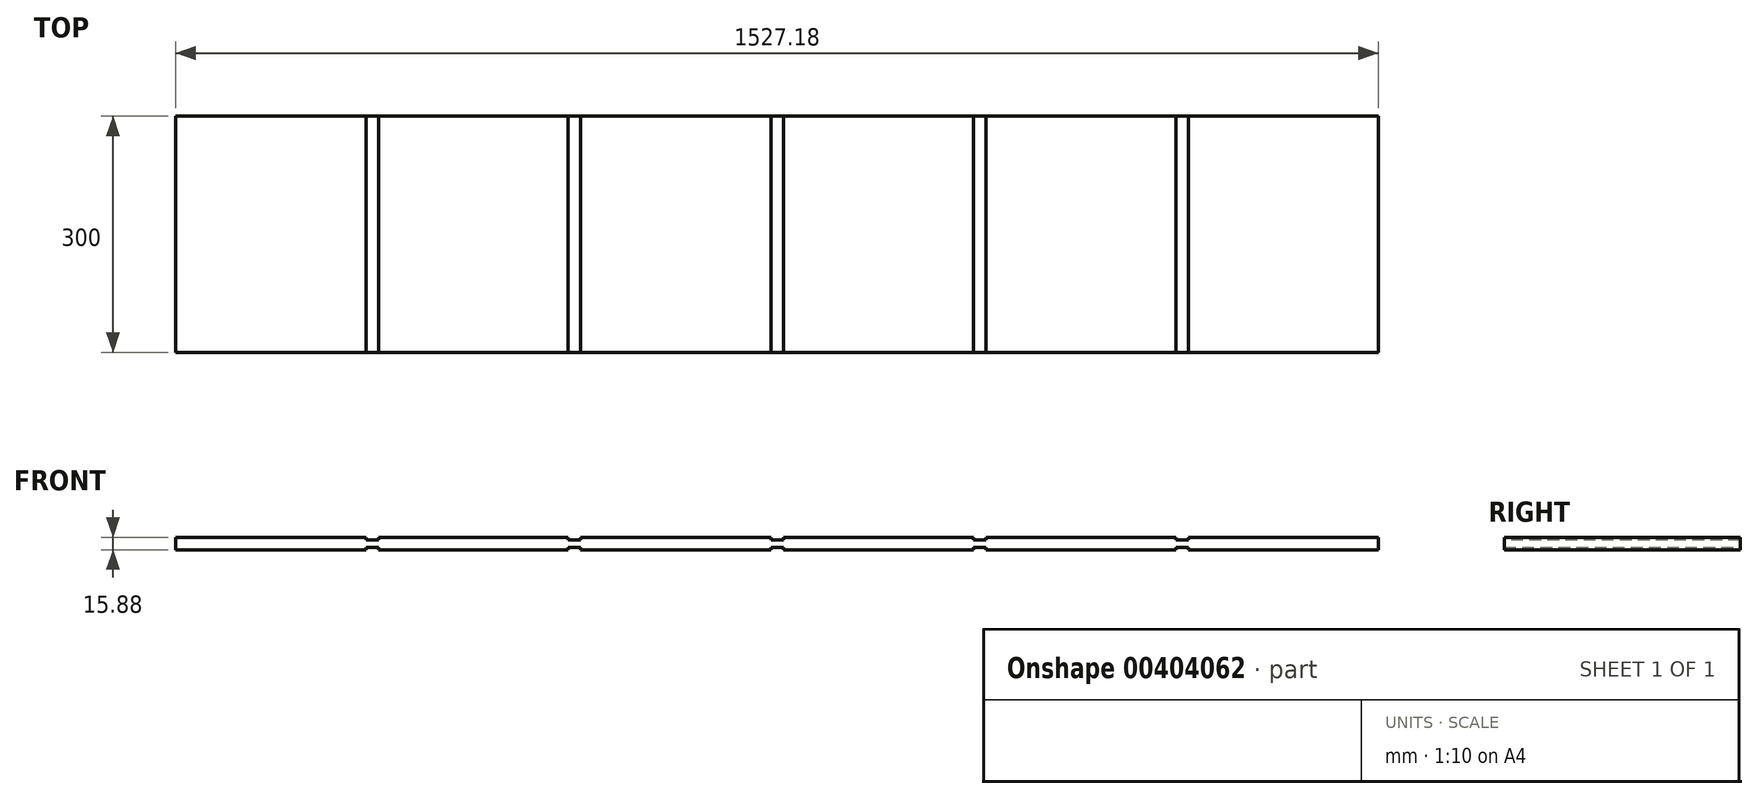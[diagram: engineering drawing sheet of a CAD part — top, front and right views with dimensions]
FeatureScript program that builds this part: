
annotation { "Feature Type Name" : "Feature", "Feature Type Description" : "" }
export const myFeature = defineFeature(function(context is Context, id is Id, definition is map)
    precondition{}
    {
        {
            var Q0;
            Q0=qCreatedBy(makeId("Front.planeOp"),FACE);
            var sketch = newSketch(context, id + "F0", { "sketchPlane" : qUnion([Q0])});
            skLineSegment(sketch, "E0.bottom", {"start": v(-761.76, -27.04) * mm, "end": v(765.42, -27.04) * mm});
            skLineSegment(sketch, "E0.top", {"start": v(-761.76, -42.92) * mm, "end": v(765.42, -42.92) * mm});
            skLineSegment(sketch, "E0.left", {"start": v(-761.76, -27.04) * mm, "end": v(-761.76, -42.92) * mm});
            skLineSegment(sketch, "E0.right", {"start": v(765.42, -27.04) * mm, "end": v(765.42, -42.92) * mm});
            skSolve(sketch);
        }
        {
            var Q0;
            Q0 = qSketchRegion(id + "F0", true);
            extrude(context, id + "F1", {"entities" : qUnion([Q0]), "depth" : 300 * mm});
        }
        {
            var Q0;
            Q0=makeQuery(id+"F1.opExtrude","SWEPT_FACE",FACE,{"disambiguationData":[OSD([sQuery(id+"F0.wireOp",EDGE,"E0.top")])]});
            var sketch = newSketch(context, id + "F2", { "sketchPlane" : qUnion([Q0])});
            skLineSegment(sketch, "E1.bottom", {"start": v(-761.76, 300) * mm, "end": v(-520.46, 300) * mm});
            skLineSegment(sketch, "E1.top", {"start": v(-761.76, 0) * mm, "end": v(-520.46, 0) * mm});
            skLineSegment(sketch, "E1.left", {"start": v(-761.76, 300) * mm, "end": v(-761.76, 0) * mm});
            skLineSegment(sketch, "E1.right", {"start": v(-520.46, 300) * mm, "end": v(-520.46, 0) * mm});
            skLineSegment(sketch, "E2.bottom", {"start": v(-504.58, 300) * mm, "end": v(-263.28, 300) * mm});
            skLineSegment(sketch, "E2.top", {"start": v(-504.58, 0) * mm, "end": v(-263.28, 0) * mm});
            skLineSegment(sketch, "E2.left", {"start": v(-504.58, 300) * mm, "end": v(-504.58, 0) * mm});
            skLineSegment(sketch, "E2.right", {"start": v(-263.28, 300) * mm, "end": v(-263.28, 0) * mm});
            skLineSegment(sketch, "E3.bottom", {"start": v(-247.4, 300) * mm, "end": v(-6.1, 300) * mm});
            skLineSegment(sketch, "E3.top", {"start": v(-247.4, 0) * mm, "end": v(-6.1, 0) * mm});
            skLineSegment(sketch, "E3.left", {"start": v(-247.4, 300) * mm, "end": v(-247.4, 0) * mm});
            skLineSegment(sketch, "E3.right", {"start": v(-6.1, 300) * mm, "end": v(-6.1, 0) * mm});
            skLineSegment(sketch, "E4.bottom", {"start": v(9.77, 300) * mm, "end": v(251.07, 300) * mm});
            skLineSegment(sketch, "E4.top", {"start": v(9.77, 0) * mm, "end": v(251.07, 0) * mm});
            skLineSegment(sketch, "E4.left", {"start": v(9.77, 300) * mm, "end": v(9.77, 0) * mm});
            skLineSegment(sketch, "E4.right", {"start": v(251.07, 300) * mm, "end": v(251.07, 0) * mm});
            skLineSegment(sketch, "E5.bottom", {"start": v(266.94, 300) * mm, "end": v(508.24, 300) * mm});
            skLineSegment(sketch, "E5.top", {"start": v(266.94, 0) * mm, "end": v(508.24, 0) * mm});
            skLineSegment(sketch, "E5.left", {"start": v(266.94, 300) * mm, "end": v(266.94, 0) * mm});
            skLineSegment(sketch, "E5.right", {"start": v(508.24, 300) * mm, "end": v(508.24, 0) * mm});
            skLineSegment(sketch, "E6.bottom", {"start": v(524.12, 300) * mm, "end": v(765.42, 300) * mm});
            skLineSegment(sketch, "E6.top", {"start": v(524.12, 0) * mm, "end": v(765.42, 0) * mm});
            skLineSegment(sketch, "E6.left", {"start": v(524.12, 300) * mm, "end": v(524.12, 0) * mm});
            skLineSegment(sketch, "E6.right", {"start": v(765.42, 300) * mm, "end": v(765.42, 0) * mm});
            skLineSegment(sketch, "E7.bottom", {"start": v(-520.46, 300) * mm, "end": v(-504.58, 300) * mm});
            skLineSegment(sketch, "E7.top", {"start": v(-520.46, 0) * mm, "end": v(-504.58, 0) * mm});
            skLineSegment(sketch, "E8.bottom", {"start": v(-263.28, 300) * mm, "end": v(-247.4, 300) * mm});
            skLineSegment(sketch, "E8.top", {"start": v(-263.28, 0) * mm, "end": v(-247.4, 0) * mm});
            skLineSegment(sketch, "E9.bottom", {"start": v(-6.1, 300) * mm, "end": v(9.77, 300) * mm});
            skLineSegment(sketch, "E9.top", {"start": v(-6.1, 0) * mm, "end": v(9.77, 0) * mm});
            skLineSegment(sketch, "E10.bottom", {"start": v(251.07, 300) * mm, "end": v(266.94, 300) * mm});
            skLineSegment(sketch, "E10.top", {"start": v(251.07, 0) * mm, "end": v(266.94, 0) * mm});
            skLineSegment(sketch, "E11.bottom", {"start": v(508.24, 300) * mm, "end": v(524.12, 300) * mm});
            skLineSegment(sketch, "E11.top", {"start": v(508.24, 0) * mm, "end": v(524.12, 0) * mm});
            skSolve(sketch);
        }
        {
            var Q0;
            Q0=makeQuery(id+"F2.imprint","IMPRINT",FACE,{"disambiguationData":[TD([[makeQuery(id+"F2.imprint","IMPRINT",EDGE,{"derivedFrom":sQuery(id+"F2.wireOp",EDGE,"E8.bottom")}),-1.0]])]});
            var Q1;
            Q1=makeQuery(id+"F2.imprint","IMPRINT",FACE,{"disambiguationData":[TD([[makeQuery(id+"F2.imprint","IMPRINT",EDGE,{"derivedFrom":sQuery(id+"F2.wireOp",EDGE,"E9.bottom")}),-1.0]])]});
            var Q2;
            Q2=makeQuery(id+"F2.imprint","IMPRINT",FACE,{"disambiguationData":[TD([[makeQuery(id+"F2.imprint","IMPRINT",EDGE,{"derivedFrom":sQuery(id+"F2.wireOp",EDGE,"E7.bottom")}),-1.0]])]});
            var Q3;
            Q3=makeQuery(id+"F2.imprint","IMPRINT",FACE,{"disambiguationData":[TD([[makeQuery(id+"F2.imprint","IMPRINT",EDGE,{"derivedFrom":sQuery(id+"F2.wireOp",EDGE,"E10.bottom")}),-1.0]])]});
            var Q4;
            Q4=makeQuery(id+"F2.imprint","IMPRINT",FACE,{"disambiguationData":[TD([[makeQuery(id+"F2.imprint","IMPRINT",EDGE,{"derivedFrom":sQuery(id+"F2.wireOp",EDGE,"E11.bottom")}),-1.0]])]});
            extrude(context, id + "F3", {"entities" : qUnion([Q0, Q1, Q2, Q3, Q4]), "operationType" : NewBodyOperationType.REMOVE, "oppositeDirection" : true, "depth" : 3.17 * mm});
        }
        {
            var Q0;
            Q0=makeQuery(id+"F1.opExtrude","SWEPT_FACE",FACE,{"disambiguationData":[OSD([sQuery(id+"F0.wireOp",EDGE,"E0.bottom")])]});
            var sketch = newSketch(context, id + "F4", { "sketchPlane" : qUnion([Q0])});
            skLineSegment(sketch, "E12.bottom", {"start": v(-520.46, 0) * mm, "end": v(-504.58, 0) * mm});
            skLineSegment(sketch, "E12.top", {"start": v(-520.46, -300) * mm, "end": v(-504.58, -300) * mm});
            skLineSegment(sketch, "E12.left", {"start": v(-520.46, 0) * mm, "end": v(-520.46, -300) * mm});
            skLineSegment(sketch, "E12.right", {"start": v(-504.58, 0) * mm, "end": v(-504.58, -300) * mm});
            skLineSegment(sketch, "E13.bottom", {"start": v(-263.28, 0) * mm, "end": v(-247.4, 0) * mm});
            skLineSegment(sketch, "E13.top", {"start": v(-263.28, -300) * mm, "end": v(-247.4, -300) * mm});
            skLineSegment(sketch, "E13.left", {"start": v(-263.28, 0) * mm, "end": v(-263.28, -300) * mm});
            skLineSegment(sketch, "E13.right", {"start": v(-247.4, 0) * mm, "end": v(-247.4, -300) * mm});
            skLineSegment(sketch, "E14.bottom", {"start": v(-6.1, 0) * mm, "end": v(9.77, 0) * mm});
            skLineSegment(sketch, "E14.top", {"start": v(-6.1, -300) * mm, "end": v(9.77, -300) * mm});
            skLineSegment(sketch, "E14.left", {"start": v(-6.1, 0) * mm, "end": v(-6.1, -300) * mm});
            skLineSegment(sketch, "E14.right", {"start": v(9.77, 0) * mm, "end": v(9.77, -300) * mm});
            skLineSegment(sketch, "E15.bottom", {"start": v(251.07, 0) * mm, "end": v(266.94, 0) * mm});
            skLineSegment(sketch, "E15.top", {"start": v(251.07, -300) * mm, "end": v(266.94, -300) * mm});
            skLineSegment(sketch, "E15.left", {"start": v(251.07, 0) * mm, "end": v(251.07, -300) * mm});
            skLineSegment(sketch, "E15.right", {"start": v(266.94, 0) * mm, "end": v(266.94, -300) * mm});
            skLineSegment(sketch, "E16.bottom", {"start": v(508.24, 0) * mm, "end": v(524.12, 0) * mm});
            skLineSegment(sketch, "E16.top", {"start": v(508.24, -300) * mm, "end": v(524.12, -300) * mm});
            skLineSegment(sketch, "E16.left", {"start": v(508.24, 0) * mm, "end": v(508.24, -300) * mm});
            skLineSegment(sketch, "E16.right", {"start": v(524.12, 0) * mm, "end": v(524.12, -300) * mm});
            skSolve(sketch);
        }
        {
            var Q0;
            Q0 = qSketchRegion(id + "F4", true);
            extrude(context, id + "F5", {"entities" : qUnion([Q0]), "operationType" : NewBodyOperationType.REMOVE, "oppositeDirection" : true, "depth" : 3.17 * mm});
        }
    });
